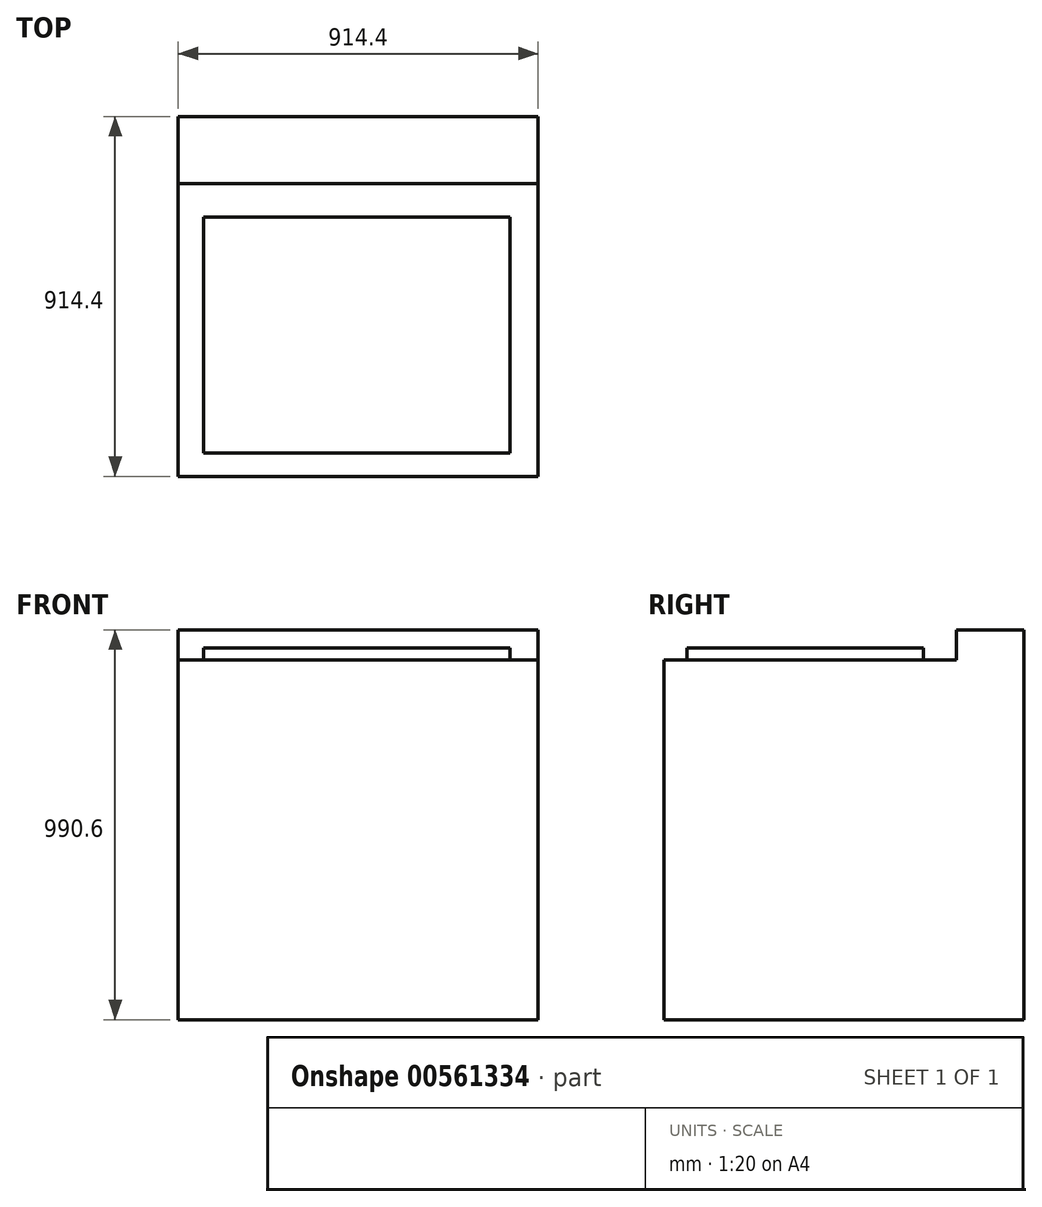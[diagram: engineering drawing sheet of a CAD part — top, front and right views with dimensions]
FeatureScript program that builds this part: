
annotation { "Feature Type Name" : "Feature", "Feature Type Description" : "" }
export const myFeature = defineFeature(function(context is Context, id is Id, definition is map)
    precondition{}
    {
        {
            var Q0;
            Q0=qCreatedBy(makeId("Top.planeOp"),FACE);
            var sketch = newSketch(context, id + "F0", { "sketchPlane" : qUnion([Q0])});
            skLineSegment(sketch, "E0.bottom", {"start": v(0, 0) * mm, "end": v(914.4, 0) * mm});
            skLineSegment(sketch, "E0.top", {"start": v(0, -914.4) * mm, "end": v(914.4, -914.4) * mm});
            skLineSegment(sketch, "E0.left", {"start": v(0, 0) * mm, "end": v(0, -914.4) * mm});
            skLineSegment(sketch, "E0.right", {"start": v(914.4, 0) * mm, "end": v(914.4, -914.4) * mm});
            skSolve(sketch);
        }
        {
            var Q0;
            Q0 = qSketchRegion(id + "F0", true);
            extrude(context, id + "F1", {"entities" : qUnion([Q0]), "depth" : 914.4 * mm, "offsetDistance" : 30.48 * mm});
        }
        {
            var Q0;
            Q0=makeQuery(id+"F1.opExtrude","CAP_FACE",FACE,{"disambiguationData":[OSD([sQuery(id+"F0.wireOp",EDGE,"E0.bottom"),sQuery(id+"F0.wireOp",EDGE,"E0.top"),sQuery(id+"F0.wireOp",EDGE,"E0.left"),sQuery(id+"F0.wireOp",EDGE,"E0.right")])],"isStart":false});
            var sketch = newSketch(context, id + "F2", { "sketchPlane" : qUnion([Q0])});
            skLineSegment(sketch, "E1.bottom", {"start": v(0, 0) * mm, "end": v(914.4, 0) * mm});
            skLineSegment(sketch, "E1.top", {"start": v(0, -171.23) * mm, "end": v(914.4, -171.23) * mm});
            skLineSegment(sketch, "E1.left", {"start": v(0, 0) * mm, "end": v(0, -171.23) * mm});
            skLineSegment(sketch, "E1.right", {"start": v(914.4, 0) * mm, "end": v(914.4, -171.23) * mm});
            skSolve(sketch);
        }
        {
            var Q0;
            Q0 = qSketchRegion(id + "F2", true);
            extrude(context, id + "F3", {"entities" : qUnion([Q0]), "operationType" : NewBodyOperationType.ADD, "depth" : 76.2 * mm, "offsetDistance" : 30.48 * mm});
        }
        {
            var Q0;
            Q0=makeQuery(id+"F1.opExtrude","CAP_FACE",FACE,{"disambiguationData":[OSD([sQuery(id+"F0.wireOp",EDGE,"E0.bottom"),sQuery(id+"F0.wireOp",EDGE,"E0.top"),sQuery(id+"F0.wireOp",EDGE,"E0.left"),sQuery(id+"F0.wireOp",EDGE,"E0.right")])],"isStart":false});
            var sketch = newSketch(context, id + "F4", { "sketchPlane" : qUnion([Q0])});
            skLineSegment(sketch, "E2.bottom", {"start": v(64.6, -255.41) * mm, "end": v(842.82, -255.41) * mm});
            skLineSegment(sketch, "E2.top", {"start": v(64.6, -855.92) * mm, "end": v(842.82, -855.92) * mm});
            skLineSegment(sketch, "E2.left", {"start": v(64.6, -255.41) * mm, "end": v(64.6, -855.92) * mm});
            skLineSegment(sketch, "E2.right", {"start": v(842.82, -255.41) * mm, "end": v(842.82, -855.92) * mm});
            skSolve(sketch);
        }
        {
            var Q0;
            Q0 = qSketchRegion(id + "F4", true);
            extrude(context, id + "F5", {"entities" : qUnion([Q0]), "operationType" : NewBodyOperationType.ADD, "depth" : 30.48 * mm, "offsetDistance" : 30.48 * mm});
        }
    });
